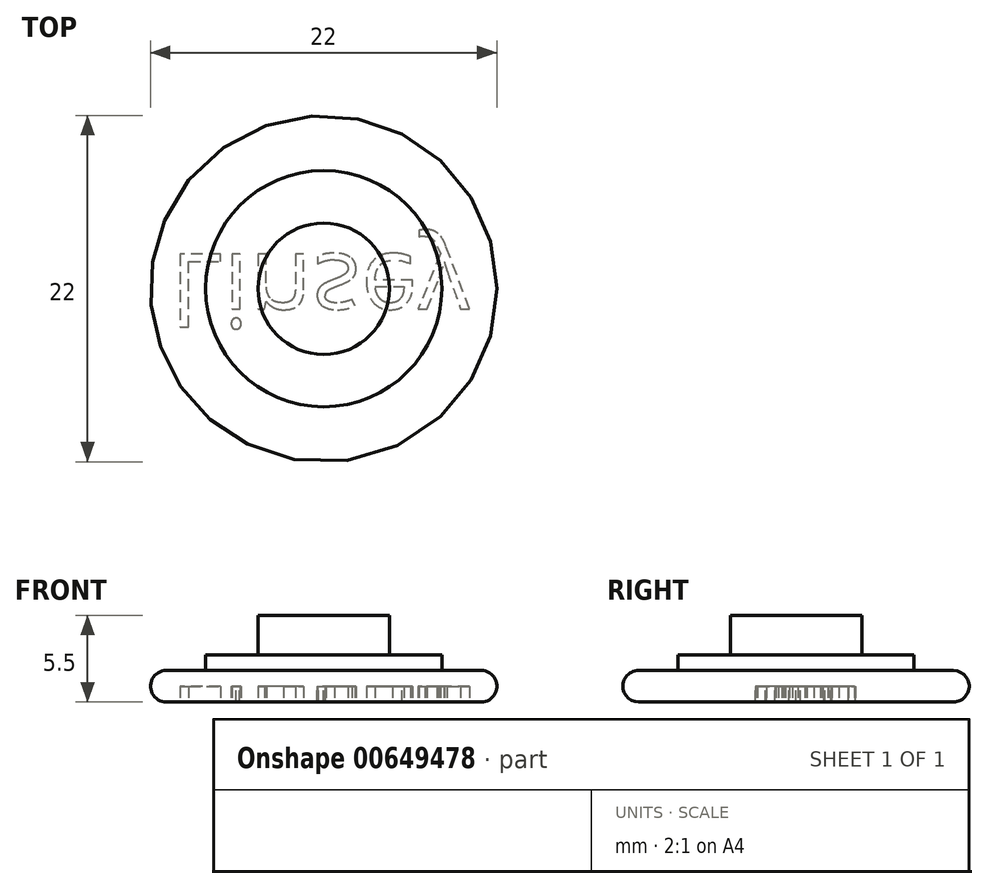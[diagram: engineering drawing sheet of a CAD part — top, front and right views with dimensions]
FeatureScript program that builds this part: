
annotation { "Feature Type Name" : "Feature", "Feature Type Description" : "" }
export const myFeature = defineFeature(function(context is Context, id is Id, definition is map)
    precondition{}
    {
        {
            var Q0;
            Q0=qCreatedBy(makeId("Top.planeOp"),FACE);
            var sketch = newSketch(context, id + "F0", { "sketchPlane" : qUnion([Q0])});
            skCircle(sketch, "E0", {"center": v(0, 0) * mm, "radius": 11 * mm});
            skCircle(sketch, "E1", {"center": v(0, 0) * mm, "radius": 7.5 * mm});
            skCircle(sketch, "E2", {"center": v(0, 0) * mm, "radius": 4.17 * mm});
            skSolve(sketch);
        }
        {
            var Q0;
            Q0=makeQuery(id+"F0.imprint","IMPRINT",FACE,{"disambiguationData":[TD([[makeQuery(id+"F0.imprint","IMPRINT",EDGE,{"derivedFrom":sQuery(id+"F0.wireOp",EDGE,"E0")}),1.0]])]});
            extrude(context, id + "F1", {"entities" : qUnion([Q0]), "depth" : 2 * mm, "offsetDistance" : 25 * mm});
        }
        {
            var Q0;
            Q0=makeQuery(id+"F0.imprint","IMPRINT",FACE,{"disambiguationData":[TD([[makeQuery(id+"F0.imprint","IMPRINT",EDGE,{"derivedFrom":sQuery(id+"F0.wireOp",EDGE,"E1")}),1.0]])]});
            extrude(context, id + "F2", {"entities" : qUnion([Q0]), "operationType" : NewBodyOperationType.ADD, "depth" : 3 * mm, "offsetDistance" : 25 * mm});
        }
        {
            var Q0;
            Q0=makeQuery(id+"F0.imprint","IMPRINT",FACE,{"disambiguationData":[TD([[makeQuery(id+"F0.imprint","IMPRINT",EDGE,{"derivedFrom":sQuery(id+"F0.wireOp",EDGE,"E2")}),1.0]])]});
            extrude(context, id + "F3", {"entities" : qUnion([Q0]), "operationType" : NewBodyOperationType.ADD, "depth" : 5.5 * mm, "offsetDistance" : 25 * mm});
        }
        {
            var Q0;
            Q0=makeQuery(id+"F1.opExtrude","CAP_EDGE",EDGE,{"disambiguationData":[OSD([sQuery(id+"F0.wireOp",EDGE,"E0")])],"isStart":false});
            var Q1;
            Q1=makeQuery(id+"F1.opExtrude","CAP_EDGE",EDGE,{"disambiguationData":[OSD([sQuery(id+"F0.wireOp",EDGE,"E0")])],"isStart":true});
            fillet(context, id + "F4", {"entities" : qUnion([Q0, Q1]), "radius" : 1 * mm, "tangentPropagation" : true, "allowEdgeOverflow" : false});
        }
        {
            var Q0;
            {var subQ0=sQuery(id+"F0.wireOp",EDGE,"E2");var subQ1=sQuery(id+"F0.wireOp",EDGE,"E1");Q0=makeQuery(id+"F3.boolean.opBoolean","MERGE",FACE,{"derivedFrom":[makeQuery(id+"F2.boolean.opBoolean","MERGE",FACE,{"derivedFrom":[makeQuery(id+"F1.opExtrude","CAP_FACE",FACE,{"disambiguationData":[OSD([sQuery(id+"F0.wireOp",EDGE,"E0"),subQ1])],"isStart":true}),makeQuery(id+"F2.opExtrude","CAP_FACE",FACE,{"disambiguationData":[OSD([subQ1,subQ0])],"isStart":true})]}),makeQuery(id+"F3.opExtrude","CAP_FACE",FACE,{"disambiguationData":[OSD([subQ0])],"isStart":true})]});}
            var sketch = newSketch(context, id + "F5", { "sketchPlane" : qUnion([Q0])});
            skText(sketch, "E3", { "text": "Linsey", "fontName": "OpenSans-Regular.ttf"});
            const initialGuessF5  = {"E3": [-0.00976, -0.0022, 1, 0, 0.00468]};
            skSetInitialGuess(sketch, initialGuessF5);
            skSolve(sketch);
        }
        {
            var Q0;
            Q0 = qSketchRegion(id + "F5", true);
            extrude(context, id + "F6", {"entities" : qUnion([Q0]), "operationType" : NewBodyOperationType.REMOVE, "oppositeDirection" : true, "depth" : 1 * mm, "offsetDistance" : 25 * mm});
        }
    });
